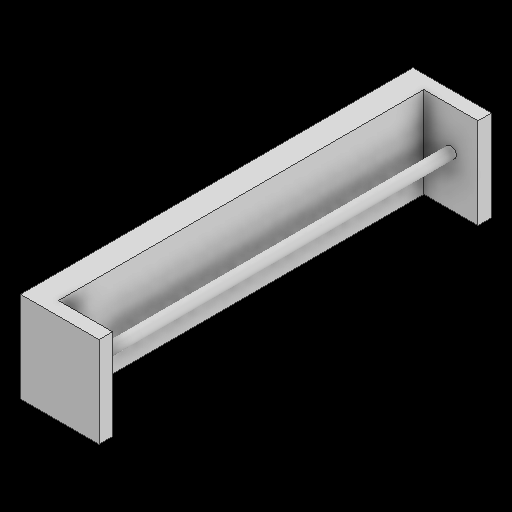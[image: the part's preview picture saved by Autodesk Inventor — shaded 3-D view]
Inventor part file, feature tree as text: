
AUTODESK INVENTOR PART (.ipt)
format: ipt  version: 2025.1 (Build 291241000, 241)  size: 126,976 bytes
history: native  units: in
note: dims shown in document units (in); Inventor stores cm internally (conversion verified against a paired STEP export)
features: extrude x3, sketch x3, projected_geometry x2, other x1
ambient origin geometry x8: Origin, YZ Plane, XZ Plane, XY Plane, X Axis, Y Axis, Z Axis, Center Point
bodies: Body1 (feature_tree)
feature tree (9):
  other  "솔리드1"
  extrude  "돌출1"  Depth=1.1417in
  extrude  "돌출2"  Depth=1.3189in
  extrude  "돌출3"  Depth=5.7087in TaperAngle=0.0deg
  sketch  "스케치1"
  sketch  "스케치2"
  projected_geometry  "투영된 루프1"
  sketch  "스케치3"
  projected_geometry  "투영된 루프2"
